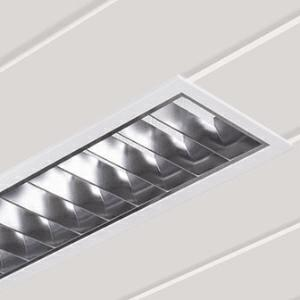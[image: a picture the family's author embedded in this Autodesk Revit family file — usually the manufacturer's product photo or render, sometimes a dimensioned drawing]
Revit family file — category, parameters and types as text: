
# Revit family: 3f_filippi_-_l_560_2s_3f_filippi_-_270933_-_l_561x24w_led_2s_221x1256
name_source: partatom
category: Lighting Fixtures
units: mm (PartAtom-declared; Revit-internal decimal feet)

## family parameters
Cut with Voids When Loaded = No
Host = Face
Light Source = No
Part Type = Normal
Room Calculation Point = No
Round Connector Dimension = Use Diameter
Shared = No

## types (1)
- 3F Filippi - L 560 2S (1 x LED, 2906 lm, 27 W, 4000 K)
    Apparent Load = 27 VA
    Approval mark = ENEC
    CIE Flux Codes = 78 98 100 100 100
    Color Rendering = 80
    Color Temperature = 4000 K
    Control Gear = Electronic ballast
    Default Elevation = 1800 mm
    Description = ILLUMINOTECHNICAL
Luminous efficiency 100% (DLOR 100%, ULOR 0%).
Initial luminous flux of the luminaire 2906 lm.
Direct symmetric distribution.
Installation Interdistance Transv.D = 0.99 x hu - Long.D = 1.04 x hu.
Average luminance <1000 cd/m² for radial angles >65°.
Tabular UGR (CIE 117 - 4H-8H; S=0.25H; 70/50/20): RUG 13.1 - 15.5.
Beam angle: 70° - 76°.
Luminous efficacy 108 lm/W.
Lifetime (L93/B10): 30000 h. (tq+25°C)
Lifetime (L90/B10): 50000 h. (tq+25°C)
Lifetime (L85/B10): 80000 h. (tq+25°C)
Lifetime (L80/B10): 100000 h. (tq+25°C)
Sudden decreased luminous flux after 50000 hours: 0% (C0).
Photobiological safety in compliance with IEC/TR 62778: RG0 risk exempt, (IEC 62471).
In compliance with IEC/EN 62722-2-1 - IEC/EN 62717 standards.

SOURCE
Linear LED module 24W/840.
Energy efficiency class (UE 2019/2020 - UE 2019/2015): D.
CIE 13.3 Colour rendering index: CRI >80 (R9 <50%).
IES TM-30 Fidelity Index: Rf = 84 Rg = 95.
CCT nominal colour temperature 4000 K.
Colour initial tolerance (MacAdam): SDCM 3.

MECHANICAL
Housing in galvannealed steel, painted in white epoxy-polyester.
2S parabolic louvre in semi-specular aluminium, non-reflecting, with transverse blades closed at the top.
Prismatic flat diffuser in transparent methacrylate (PMMA), multilenticular, anti-glare, prismatic exterior, placed above louvre blades.
Film protective against dust and finger marks, adhesive, attached to louvre.
Luminaire with limited surface temperature. - D - (EN 60598-2-24)
Dimensions: 1256x221 mm, height 95 mm. Weight 4.535 kg.
IP20 protection degree.
Mechanical strength to impacts IK02 (0.2 joule).
Glow-wire test resistance 650°C.

ELECTRICAL
Halogen Free electronic wiring 230V-50/60Hz, power factor 0.90, THD <25%, constant output current, SELV, class I, 1 driver.
Power of the luminaire 27 W.
CE - IEC 60598-1 - EN 60598-1.
SAFE FLICKER: PstLM=<1 and SVM=<0.4 (IEC TR 61547-1 and IEC TR 63158), to ensure a more comfortable and safe light.
Luminaire compliant with EN 60598-2-22 for power supply from a centralised emergency system CPSS (Central Power Supply System), not incorporated in the luminaire - high risk areas excluded. The default power and flux are 100% in AC and 100% in DC.
Ambient temperature from 0°C to +25°C.
Temperature class T6 max 85°C.
Relative humidity UR: <85%.

INSTALLATION
Pull-up recessed fitting / Slat ceiling recessed fitting.
False ceiling carving: 190x1230 mm.
All accessories dedicated to this product are available on the Catalog and on our website www.3F-Filippi.com.

APPLICATIONS
In environments with VDTs, managerial offices and staterooms, public offices and schools.

WARNING
Luminaire designed for disposal/recycling at end-of-life.
Replaceable (LED only) light source by a professional. Replaceable control gear by a professional.
    Height = 0 mm  [stored 0 ft]
    Lamp = 1 x LED
    Lamp Light Flux = 2906 lm
    Lamp Power = 27 W
    Lamp count = 1
    Length = 1256 mm
    Lifetime = 50000 h
    Luminous efficacy = 108 lm/W
    Manufacturer = 3F Filippi
    ModVariant = No
    Model = 3F Filippi - 270933 - L 561x24W LED 2S 221x1256
    Mounting Place = Ceiling
    Mounting Type = Recessed
    Number of Poles = 1
    OnlyDefault = Yes
    Power Factor = 1
    Product Name = 3F Filippi - L 560 2S
    Product group = recessed luminaire
    ProductGroupID = 4
    Protection Class = Protection class I
    Protection Degree = IP 20
    RLX_Detail_Level = 1
    RLX_Emergency_Light_Flux = 0 lm
    RLX_Emergency_Type = 0
    RLX_Emergency_Type_DB = No
    RlxData = <blob elided: 60581 chars, md5=5ef84f0f>
    Socket = socket
    Standby Power = 0 W
    System Light Flux = 2906 lm
    System Power = 27 W
    Type Comments = Product without accessories
    Type Image = 3ffilippi_270933.jpg
    URL = http://relux.com
    VarID = ---
    Voltage = 0 V
    Weight = 0.00 kg
    Width = 221 mm

note: [stored X ft] marks values corroborated as IEEE doubles in the binary element streams (Revit-internal decimal feet)

## geometry (parser evidence)
native form markers: Blend x4, Sweep x9
no freeform markers — native parametric forms only
